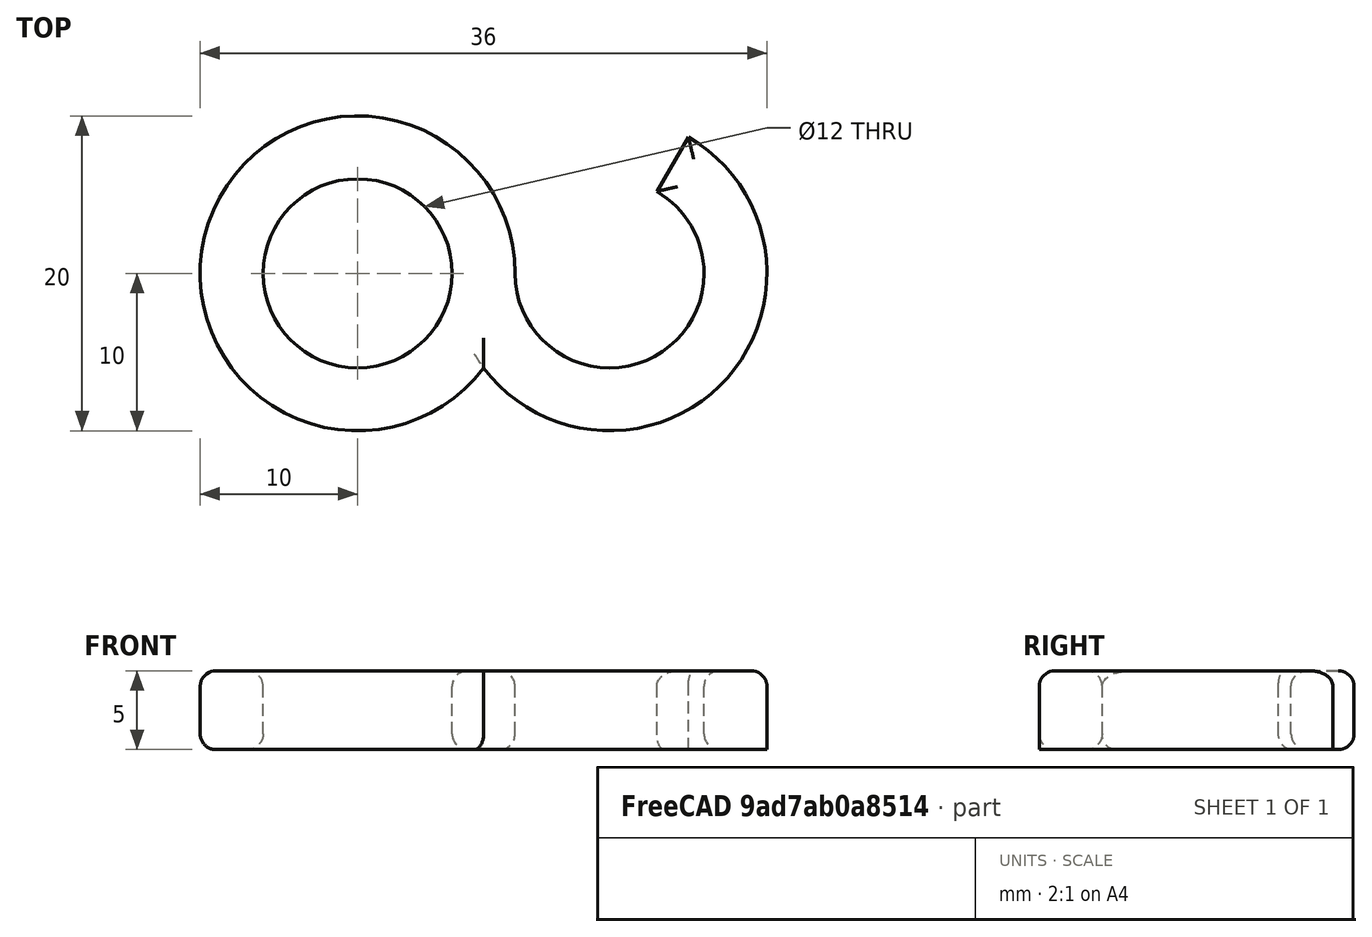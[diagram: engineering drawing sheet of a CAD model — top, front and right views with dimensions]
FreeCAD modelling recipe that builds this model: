
FCSTD DOCUMENT  (FreeCAD 0.16R6706 (Git))
Label: small_hook
License: All rights reserved
LicenseURL: http://en.wikipedia.org/wiki/All_rights_reserved
objects: Part::Cylinder×4, Part::Fillet×3, Part::Cut×2, Part::MultiFuse×1
note: 10 computed .brp shape members not serialized (recipe doc carries the construction recipe); baked Part::Feature solids carry a one-line shape summary decoded from their .brp

FEATURE [Part::Cylinder] Cylinder  label="base"
  Angle = 360
  Height = 5
  Radius = 10
FEATURE [Part::Cylinder] Cylinder001  label="resta_base"
  Angle = 360
  Height = 10
  Placement = pos=(0,0,-3) rot=(0,0,1;0rad)
  Radius = 6
FEATURE [Part::Cylinder] Cylinder002  label="garfio"
  Angle = 240
  Height = 5
  Placement = pos=(16,0,0) rot=(0,0,1;3.14159rad)
  Radius = 10
FEATURE [Part::Cylinder] Cylinder003  label="resta_garfio"
  Angle = 360
  Height = 10
  Placement = pos=(16,0,-3) rot=(0,0,1;0rad)
  Radius = 6
FEATURE [Part::Cut] Cut  label="base_hueca"
  Base = -> Cylinder
  Tool = -> Cylinder001
FEATURE [Part::Cut] Cut001  label="garfio_hueco"
  Base = -> Cylinder002
  Tool = -> Cylinder003
FEATURE [Part::MultiFuse] Fusion  label="garfio_sin_biseles"
  Shapes = -> [Cut,Cut001]
FEATURE [Part::Fillet] Fillet
  Base = -> Fusion
  Edges = 5 edges r=1: [Edge1,Edge5,Edge9,Edge11,Edge13]
FEATURE [Part::Fillet] Fillet001
  Base = -> Fillet
  Edges = 2 edges r=1: [Edge14,Edge25]
FEATURE [Part::Fillet] Fillet002
  Base = -> Fillet001
  Edges = 1 edges r=1: [Edge6]
